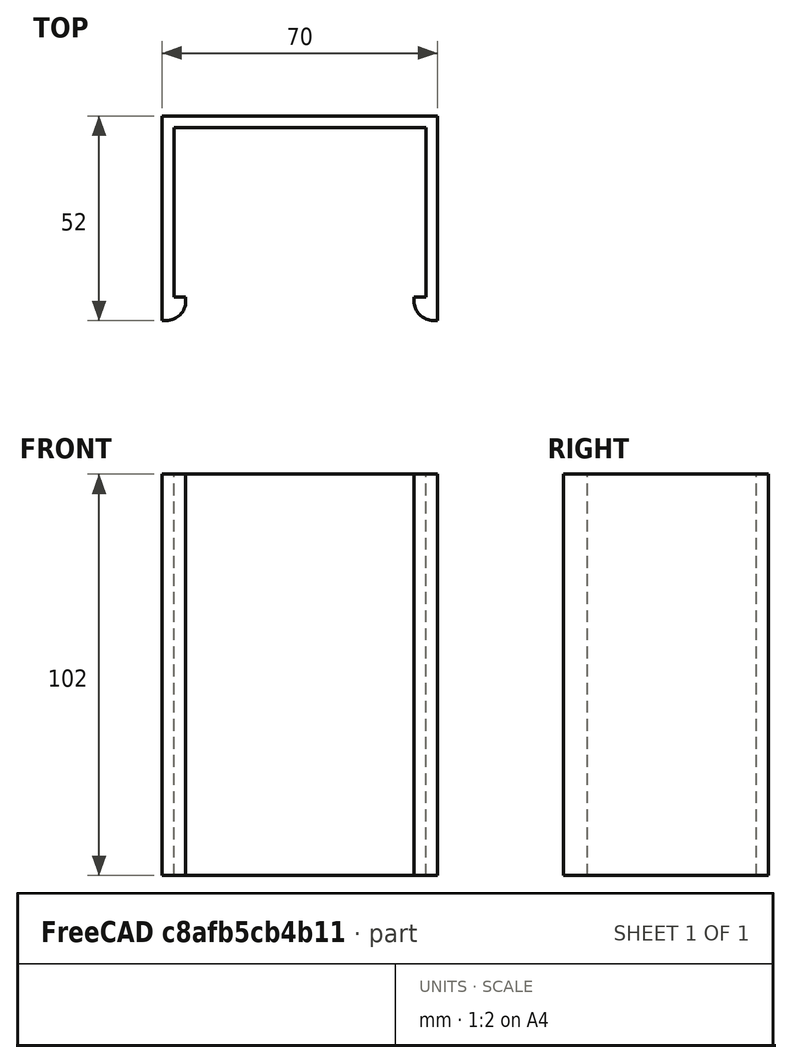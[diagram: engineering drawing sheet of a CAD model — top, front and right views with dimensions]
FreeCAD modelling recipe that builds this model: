
FCSTD DOCUMENT
Label: RemoteHeadVMount
objects: Part::Box×3, Sketcher::SketchObject×2, Part::Cut×1, Part::Fillet×1, Part::Mirroring×1, Part::MultiFuse×1
note: 9 computed .brp shape members not serialized (recipe doc carries the construction recipe); baked Part::Feature solids carry a one-line shape summary decoded from their .brp

FEATURE [Part::Box] Box
  Height = 102
  Length = 70
  Width = 46
FEATURE [Part::Box] Box001
  Height = 102
  Length = 64
  Placement = pos=(3,0,0) rot=(0,0,1;0rad)
  Width = 43
FEATURE [Part::Cut] Cut
  Base = -> Box
  Tool = -> Box001
FEATURE [Part::Box] Box002
  Height = 102
  Length = 6
  Placement = pos=(0,-6,0) rot=(0,0,1;0rad)
  Width = 6
FEATURE [Part::Fillet] Fillet
  Base = -> Box002
  Edges = 1 edges r=5: [Edge5]
FEATURE [Part::Mirroring] Part__Mirroring  label="Fillet (Mirror #1)"
  Base = (0,0,0)
  Normal = (1,0,0)
  Placement = pos=(70,0,0) rot=(0,0,1;0rad)
  Source = -> Fillet
FEATURE [Part::MultiFuse] Fusion
  Shapes = -> [Cut,Fillet,Part__Mirroring]
FEATURE [Sketcher::SketchObject] Sketch
  Placement = pos=(0,46,0) rot=(0,0.707107,0.707107;3.14159rad)
  Support = -> Fusion [Face1]
FEATURE [Sketcher::SketchObject] Sketch001
  Placement = pos=(0,46,0) rot=(0,0.707107,0.707107;3.14159rad)
  Support = -> Fusion [Face1]
  sketch-geometry (2):
    g0: Circle CenterX=-13 CenterY=87 CenterZ=0 NormalX=0 NormalY=0 NormalZ=1 Radius=2.03591
    g1: Circle CenterX=-53 CenterY=87 CenterZ=0 NormalX=0 NormalY=0 NormalZ=1 Radius=2
